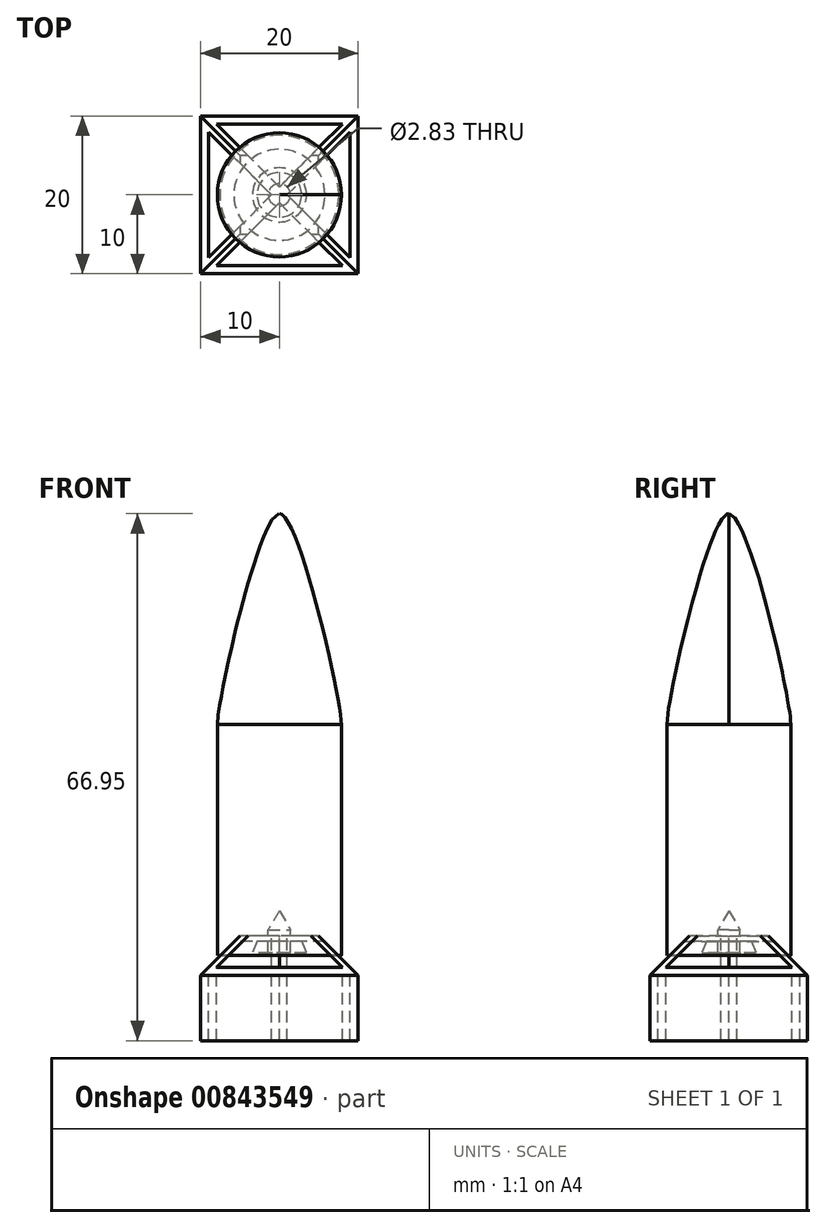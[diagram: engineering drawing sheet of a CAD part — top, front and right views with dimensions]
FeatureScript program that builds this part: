
annotation { "Feature Type Name" : "Feature", "Feature Type Description" : "" }
export const myFeature = defineFeature(function(context is Context, id is Id, definition is map)
    precondition{}
    {
        {
            var Q0;
            Q0=qCreatedBy(makeId("Front.planeOp"),FACE);
            var sketch = newSketch(context, id + "F0", { "sketchPlane" : qUnion([Q0])});
            skLineSegment(sketch, "E0", {"start": v(5.78, -29.39) * mm, "end": v(7.57, -31.17) * mm});
            skLineSegment(sketch, "E1", {"start": v(7.88, -31.17) * mm, "end": v(7.88, -1.84) * mm});
            skLineSegment(sketch, "E2", {"start": v(0, 24.95) * mm, "end": v(0, 0) * mm});
            skFitSpline(sketch, "E3", {"points": [v(0, 24.95) * mm, v(7.88, -1.84) * mm], "startDerivative": vector(7.68, 0) * mm, "endDerivative": vector(0, -9.46) * mm});
            skLineSegment(sketch, "E4", {"start": v(0, 0) * mm, "end": v(0, -25.5) * mm});
            skLineSegment(sketch, "E5", {"start": v(1.41, -30.86) * mm, "end": v(3.44, -30.86) * mm});
            skLineSegment(sketch, "E6", {"start": v(3.44, -30.86) * mm, "end": v(2.84, -29.39) * mm});
            skLineSegment(sketch, "E7", {"start": v(2.84, -29.39) * mm, "end": v(5.78, -29.39) * mm});
            skLineSegment(sketch, "E8", {"start": v(1.41, -30.86) * mm, "end": v(1.41, -27.93) * mm});
            skLineSegment(sketch, "E9", {"start": v(7.88, -31.17) * mm, "end": v(7.57, -31.17) * mm});
            skLineSegment(sketch, "E10", {"start": v(1.41, -27.93) * mm, "end": v(0, -25.5) * mm});
            skSolve(sketch);
        }
        {
            var Q0;
            Q0 = qSketchRegion(id + "F0", true);
            var Q1;
            Q1=sQuery(id+"F0.wireOp",EDGE,"E2");
            revolve(context, id + "F1", {"surfaceOperationType" : NewSurfaceOperationType.NEW, "entities" : qUnion([Q0]), "axis" : qUnion([Q1]), "revolveType" : RevolveType.FULL});
        }
        {
            var Q0;
            Q0=qCreatedBy(makeId("Top.planeOp"),FACE);
            var sketch = newSketch(context, id + "F2", { "sketchPlane" : qUnion([Q0])});
            skLineSegment(sketch, "E11.bottom", {"start": v(10, -10) * mm, "end": v(-10, -10) * mm});
            skLineSegment(sketch, "E11.top", {"start": v(10, 10) * mm, "end": v(-10, 10) * mm});
            skLineSegment(sketch, "E11.left", {"start": v(10, -10) * mm, "end": v(10, 10) * mm});
            skLineSegment(sketch, "E11.right", {"start": v(-10, -10) * mm, "end": v(-10, 10) * mm});
            skPoint(sketch, "E11.middle", {"position": v(0, 0) * mm});
            skLineSegment(sketch, "E12.0", {"start": v(8, -9) * mm, "end": v(-8, -9) * mm});
            skLineSegment(sketch, "E12.1", {"start": v(9, -8) * mm, "end": v(9, 8) * mm});
            skLineSegment(sketch, "E12.3", {"start": v(-9, -8) * mm, "end": v(-9, 8) * mm});
            skLineSegment(sketch, "E13", {"start": v(9, -8) * mm, "end": v(1, 0) * mm});
            skLineSegment(sketch, "E14", {"start": v(-9, 8) * mm, "end": v(-1, 0) * mm});
            skLineSegment(sketch, "E15", {"start": v(8, 9) * mm, "end": v(0, 1) * mm});
            skLineSegment(sketch, "E16", {"start": v(-8, -9) * mm, "end": v(0, -1) * mm});
            skLineSegment(sketch, "E17.trimOffspring", {"start": v(-1, 0) * mm, "end": v(-9, -8) * mm});
            skLineSegment(sketch, "E18.trimOffspring", {"start": v(0, 1) * mm, "end": v(-8, 9) * mm});
            skLineSegment(sketch, "E19.trimOffspring", {"start": v(1, 0) * mm, "end": v(9, 8) * mm});
            skLineSegment(sketch, "E20.trimOffspring", {"start": v(0, -1) * mm, "end": v(8, -9) * mm});
            skLineSegment(sketch, "E21", {"start": v(8, 9) * mm, "end": v(-8, 9) * mm});
            skSolve(sketch);
        }
        {
            var Q0;
            Q0=makeQuery(id+"F2.imprint","IMPRINT",FACE,{"disambiguationData":[TD([[makeQuery(id+"F2.imprint","IMPRINT",EDGE,{"derivedFrom":sQuery(id+"F2.wireOp",EDGE,"E11.bottom")}),-1.0]])]});
            extrude(context, id + "F3", {"entities" : qUnion([Q0]), "oppositeDirection" : true, "depth" : 42 * mm, "offsetDistance" : 25 * mm, "hasSecondDirection" : true, "secondDirectionOppositeDirection" : true, "secondDirectionDepth" : 28.7 * mm});
        }
        {
            var Q0;
            Q0=makeQuery(id+"F3.opExtrude","CAP_EDGE",EDGE,{"disambiguationData":[OSD([sQuery(id+"F2.wireOp",EDGE,"E11.left")])],"isStart":true});
            var Q1;
            Q1=makeQuery(id+"F3.opExtrude","CAP_EDGE",EDGE,{"disambiguationData":[OSD([sQuery(id+"F2.wireOp",EDGE,"E11.top")])],"isStart":true});
            var Q2;
            Q2=makeQuery(id+"F3.opExtrude","CAP_EDGE",EDGE,{"disambiguationData":[OSD([sQuery(id+"F2.wireOp",EDGE,"E11.right")])],"isStart":true});
            var Q3;
            Q3=makeQuery(id+"F3.opExtrude","CAP_EDGE",EDGE,{"disambiguationData":[OSD([sQuery(id+"F2.wireOp",EDGE,"E11.bottom")])],"isStart":true});
            chamfer(context, id + "F4", {"entities" : qUnion([Q0, Q1, Q2, Q3]), "width" : 5 * mm, "tangentPropagation" : true});
        }
    });
